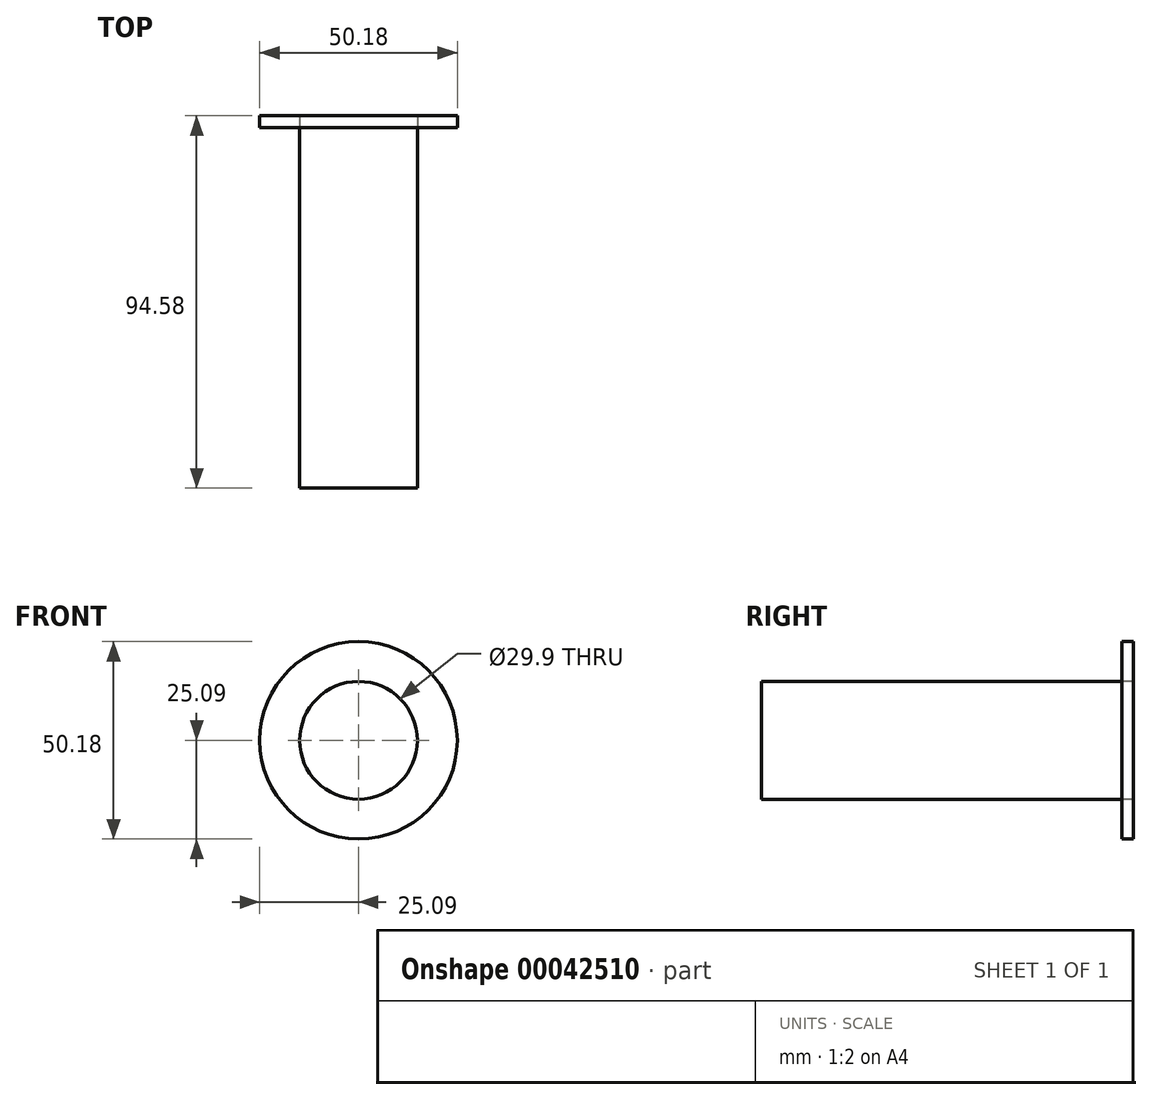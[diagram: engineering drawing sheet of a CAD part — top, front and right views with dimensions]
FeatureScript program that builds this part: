
annotation { "Feature Type Name" : "Feature", "Feature Type Description" : "" }
export const myFeature = defineFeature(function(context is Context, id is Id, definition is map)
    precondition{}
    {
        {
            var Q0;
            Q0=qCreatedBy(makeId("Front.planeOp"),FACE);
            var sketch = newSketch(context, id + "F0", { "sketchPlane" : qUnion([Q0])});
            skCircle(sketch, "E0", {"center": v(0, 0) * mm, "radius": 14.95 * mm});
            skSolve(sketch);
        }
        {
            var Q0;
            Q0=makeQuery(id+"F0.imprint","IMPRINT",FACE,{"disambiguationData":[TD([[makeQuery(id+"F0.imprint","IMPRINT",EDGE,{"derivedFrom":sQuery(id+"F0.wireOp",EDGE,"E0")}),1.0]])]});
            extrude(context, id + "F1", {"entities" : qUnion([Q0]), "depth" : 91.58 * mm});
        }
        {
            var Q0;
            Q0=makeQuery(id+"F1.opExtrude","CAP_FACE",FACE,{"disambiguationData":[OSD([sQuery(id+"F0.wireOp",EDGE,"E0")])],"isStart":true});
            var sketch = newSketch(context, id + "F2", { "sketchPlane" : qUnion([Q0])});
            skCircle(sketch, "E1", {"center": v(0, 0) * mm, "radius": 25.09 * mm});
            skCircle(sketch, "E2", {"center": v(0, 0) * mm, "radius": 32.18 * mm});
            skCircle(sketch, "E3", {"center": v(0, 0) * mm, "radius": 14.59 * mm});
            skSolve(sketch);
        }
        {
            var Q0;
            Q0=makeQuery(id+"F2.imprint","IMPRINT",FACE,{"disambiguationData":[TD([[makeQuery(id+"F2.imprint","IMPRINT",EDGE,{"derivedFrom":sQuery(id+"F2.wireOp",EDGE,"E1")}),1.0]])]});
            extrude(context, id + "F3", {"entities" : qUnion([Q0]), "depth" : 3 * mm});
        }
    });
